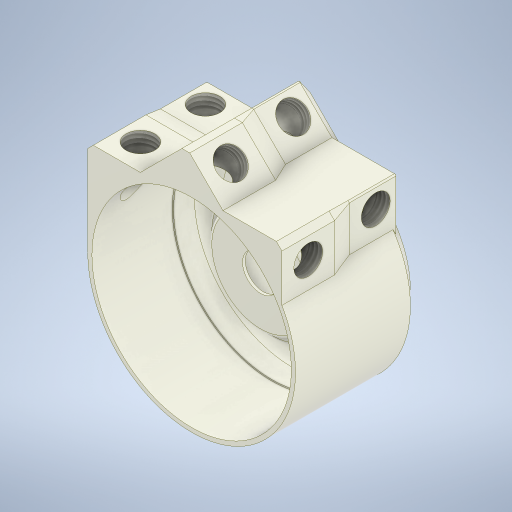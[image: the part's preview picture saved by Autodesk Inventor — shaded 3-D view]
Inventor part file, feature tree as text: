
AUTODESK INVENTOR PART (.ipt)
format: ipt  version: 2023.1 (Build 271208000, 208)  size: 770,048 bytes
history: native  units: mm
features: sketch x22, extrude x14, projected_geometry x9, hole x7, chamfer x6, fillet x2, plane x2, pattern_circular x2, other x2, revolve x1, loft x1
ambient origin geometry x8: Origin, YZ Plane, XZ Plane, XY Plane, X Axis, Y Axis, Z Axis, Center Point
bodies: Solid1 (feature_tree)
feature tree (68):
  extrude  "Extrusion1"  Depth=115.0mm TaperAngle=0.0deg
  extrude  "Extrusion2"  Depth=41.2mm TaperAngle=0.0deg
  extrude  "Extrusion3"  Depth=33.2mm TaperAngle=0.0deg
  revolve  "Revolution1"  [1 undecoded]
  extrude  "Extrusion4"  Depth=2.0mm
  fillet  "Fillet1"  Radius=2.0mm
  fillet  "Fillet2"  Radius=3.0mm
  hole  "Hole1"  [1 undecoded]
  plane  "Work Plane4"
  extrude  "Extrusion16"  Depth=26.0mm
  chamfer  "Chamfer1"  [1 undecoded]
  pattern_circular  "Circular Pattern1"  Count=8 Angle=360.0deg
  sketch  "Sketch8"  dims[d18=90.0deg d19=26.0mm d20=0.0mm d21=0.0mm]
  extrude  "Extrusion5"  Depth=38.0mm
  plane  "Work Plane1"
  extrude  "Extrusion6"  TaperAngle=0.0deg  [1 undecoded]
  pattern_circular  "Circular Pattern2"  Count=3 Angle=90.0deg
  extrude  "Extrusion7"  Depth=10.0mm
  extrude  "Extrusion8"  Depth=19.0mm
  extrude  "Extrusion9"  Depth=33.2mm TaperAngle=0.0deg
  extrude  "Extrusion10"  Depth=10.0mm TaperAngle=0.0deg
  extrude  "Extrusion11"  Depth=10.0mm TaperAngle=0.0deg
  extrude  "Extrusion12"  Depth=10.0mm TaperAngle=0.0deg
  hole  "Hole4"  [1 undecoded]
  hole  "Hole5"  [1 undecoded]
  hole  "Hole6"  [1 undecoded]
  hole  "Hole7"  [1 undecoded]
  hole  "Hole8"  [1 undecoded]
  hole  "Hole9"  [1 undecoded]
  extrude  "Extrusion15"  Depth=10.0mm TaperAngle=45.0deg
  chamfer  "Chamfer3"  Distance=25.0mm
  chamfer  "Chamfer4"  [1 undecoded]
  chamfer  "Chamfer5"  Distance=9.4mm
  chamfer  "Chamfer6"  Distance=10.0mm
  chamfer  "Chamfer7"  Angle=90.0deg  [1 undecoded]
  loft  "Loft1"
  sketch  "Sketch2"  dims[d0=150.0mm d1=115.0mm d2=0.0mm]
  sketch  "Sketch3"  dims[d3=70.4mm d4=41.2mm d5=0.0mm]
  sketch  "Sketch4"  dims[d6=86.4mm d7=33.2mm d8=0.0mm]
  sketch  "Sketch5"  dims[d9=10.0mm d10=2.0mm]
  sketch  "Sketch6"  dims[d11=2.0mm d12=2.0mm d13=2.0mm d14=3.0mm]
  sketch  "Sketch7"  dims[d16=4.886922mm d17=20.0mm]
  sketch  "Sketch9"  dims[d22=10.0mm]
  sketch  "Sketch10"  dims[d23=2.0mm]
  projected_geometry  "Projected Loop1"
  projected_geometry  "Projected Loop2"
  sketch  "Sketch11"  dims[d24=112.0mm]
  projected_geometry  "Projected Loop3"
  sketch  "Sketch12"  dims[d25=4.2mm d26=8.0mm d27=4.0mm d28=2.0mm d29=90.0deg d30=8.5mm d31=0.0mm]
  projected_geometry  "Projected Loop4"
  sketch  "Sketch13"  dims[d32=0.5mm d33=2.0mm d34=45.0deg d35=80.0mm d36=360.0deg]
  projected_geometry  "Projected Loop5"
  sketch  "Sketch14"  dims[d38=38.0mm d39=38.0mm]
  projected_geometry  "Projected Loop6"
  sketch  "Sketch15"  dims[d40=10.0mm d41=0.0mm d42=0.0mm]
  projected_geometry  "Projected Loop7"
  sketch  "Sketch24"  dims[d43=21.0mm]
  sketch  "Sketch25"  dims[d44=38.0mm]
  other  "Edges1"
  other  "Edges2"
  sketch  "Sketch27"  dims[d45=38.0mm]
  sketch  "Sketch28"  dims[d46=33.2mm d47=0.0mm d48=30.0mm d49=90.0deg]
  sketch  "Sketch29"  dims[d51=10.0mm d53=12.5mm]
  sketch  "Sketch30"  dims[d54=21.0mm d55=19.0mm]
  sketch  "Sketch31"  dims[d56=19.0mm d57=33.2mm d58=0.0mm]
  sketch  "Sketch32"  dims[d59=33.2mm d60=0.0mm d61=33.2mm d62=0.0mm d63=33.2mm d64=0.0mm d65=33.2mm d66=0.0mm d67=0.0mm d68=0.0mm d144=33.2mm d145=0.0mm d146=8.0mm d147=2.0mm d148=45.0deg d149=10.0mm d150=2.0mm d151=45.0deg d152=5.0mm d153=2.0mm d154=45.0deg d155=1.0mm d156=2.0mm d157=45.0deg d158=4.0mm d159=2.0mm d160=45.0deg d161=25.0mm d162=-5.0mm d163=9.4mm d164=10.0mm d165=0.0mm d166=0.0mm d167=90.0deg d168=0.0mm d169=90.0deg d170=1.0mm d171=45.0mm d172=11.5mm d180=20.752mm d181=10.0mm d182=4.0mm d183=2.0mm d184=90.0deg d185=61.1mm d186=20.594885mm d187=20.752mm d188=10.0mm d189=4.0mm d190=2.0mm d191=90.0deg d192=61.1mm d193=20.594885mm d194=20.752mm d195=10.0mm d196=4.0mm d197=2.0mm d198=90.0deg d199=61.1mm d200=20.594885mm d201=20.752mm d202=10.0mm d203=4.0mm d204=2.0mm d205=90.0deg d206=61.1mm d207=20.594885mm d208=20.752mm d209=10.0mm d210=4.0mm d211=2.0mm d212=90.0deg d213=61.1mm d214=20.594885mm d215=20.752mm d216=10.0mm d217=4.0mm d218=2.0mm d219=90.0deg d220=61.1mm d221=20.594885mm]
  projected_geometry  "Project Cut Edges1"
  projected_geometry  "Project Cut Edges2"
note: 12 required parameter values undecoded (feature->parameter linkage not recoverable at this tier; creation-order binding heuristic only, values carry confidence <= 0.55)